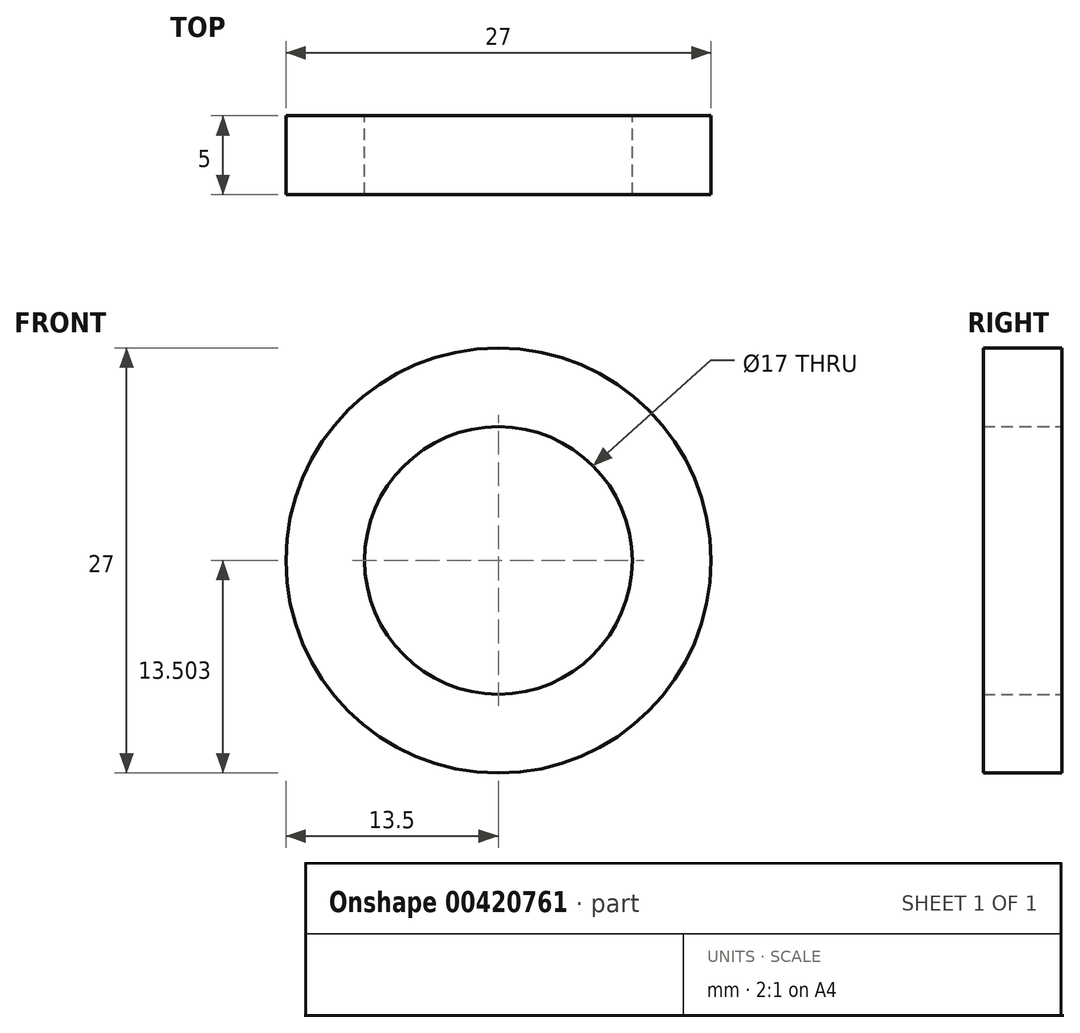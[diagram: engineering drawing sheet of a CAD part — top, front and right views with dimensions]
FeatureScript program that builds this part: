
annotation { "Feature Type Name" : "Feature", "Feature Type Description" : "" }
export const myFeature = defineFeature(function(context is Context, id is Id, definition is map)
    precondition{}
    {
        {
            var Q0;
            Q0=qCreatedBy(makeId("Front.planeOp"),FACE);
            var sketch = newSketch(context, id + "F0", { "sketchPlane" : qUnion([Q0])});
            skCircle(sketch, "E0", {"center": v(0, -0.77) * mm, "radius": 13.5 * mm});
            skCircle(sketch, "E1", {"center": v(0, -0.77) * mm, "radius": 8.5 * mm});
            skSolve(sketch);
        }
        {
            var Q0;
            Q0 = qSketchRegion(id + "F0", true);
            extrude(context, id + "F1", {"entities" : qUnion([Q0]), "depth" : 5 * mm});
        }
    });
